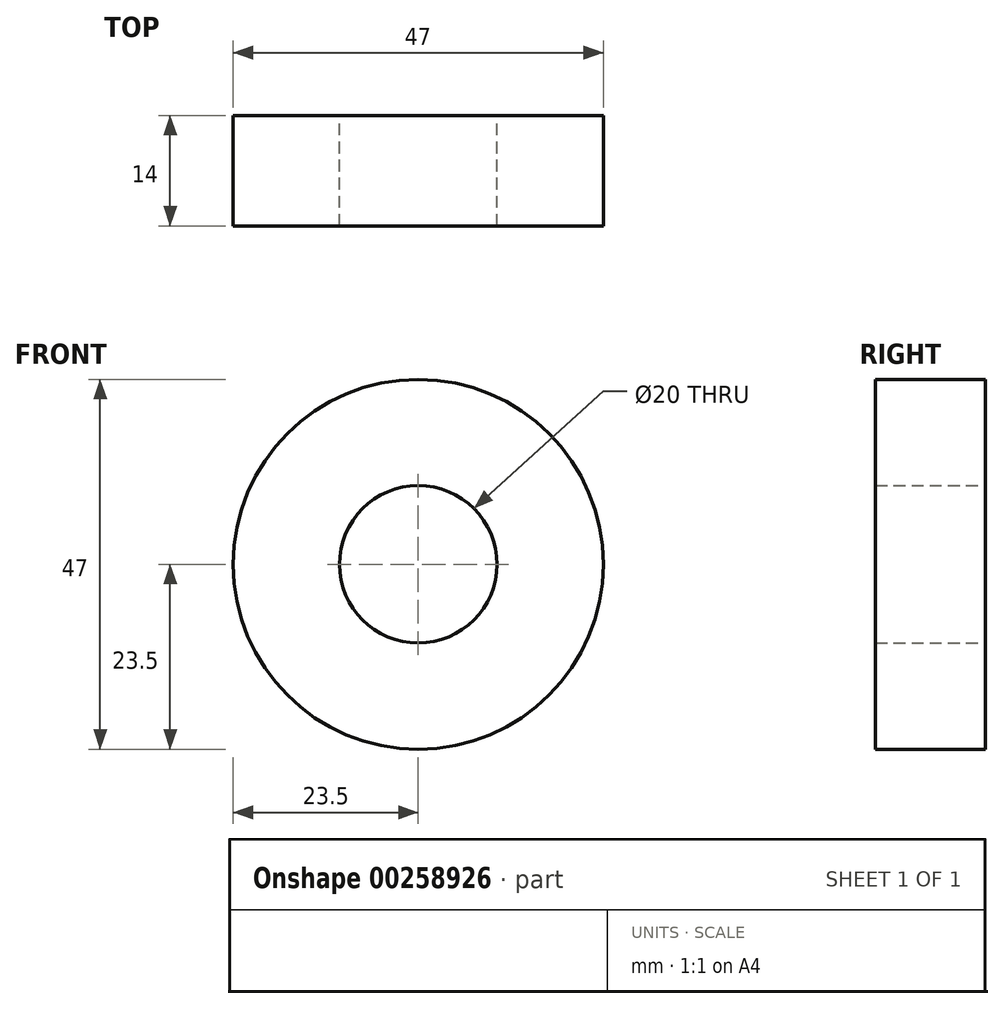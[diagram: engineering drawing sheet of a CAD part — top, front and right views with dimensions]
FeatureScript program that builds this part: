
annotation { "Feature Type Name" : "Feature", "Feature Type Description" : "" }
export const myFeature = defineFeature(function(context is Context, id is Id, definition is map)
    precondition{}
    {
        {
            var Q0;
            Q0=qCreatedBy(makeId("Front.planeOp"),FACE);
            var sketch = newSketch(context, id + "F0", { "sketchPlane" : qUnion([Q0])});
            skCircle(sketch, "E0", {"center": v(0, 0) * mm, "radius": 23.5 * mm});
            skCircle(sketch, "E1", {"center": v(0, 0) * mm, "radius": 10 * mm});
            skSolve(sketch);
        }
        {
            var Q0;
            Q0=makeQuery(id+"F0.imprint","IMPRINT",FACE,{"disambiguationData":[TD([[makeQuery(id+"F0.imprint","IMPRINT",EDGE,{"derivedFrom":sQuery(id+"F0.wireOp",EDGE,"E0")}),1.0]])]});
            extrude(context, id + "F1", {"entities" : qUnion([Q0]), "depth" : 14 * mm});
        }
    });
